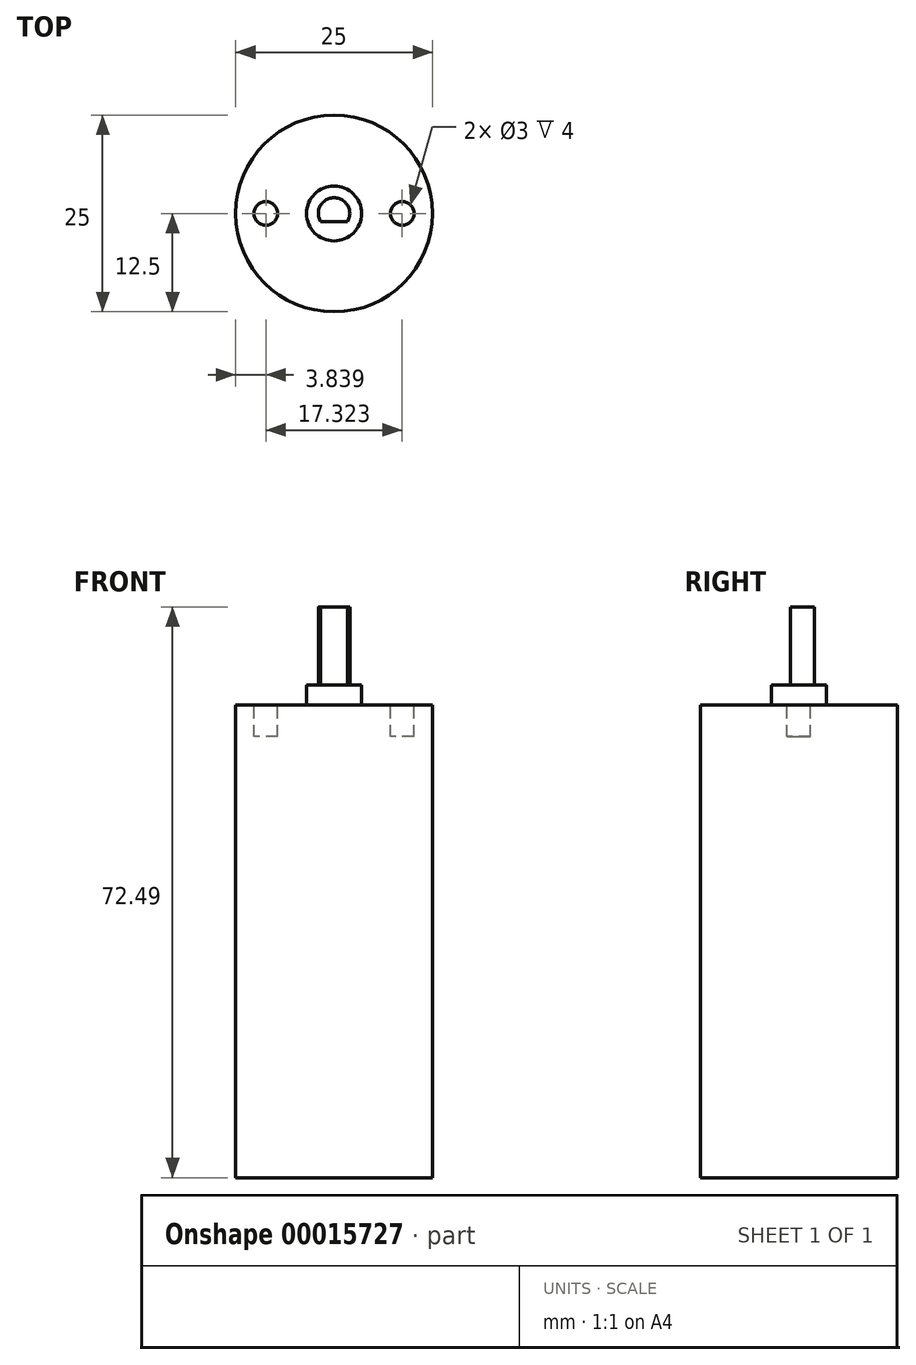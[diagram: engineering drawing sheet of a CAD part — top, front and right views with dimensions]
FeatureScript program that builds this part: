
annotation { "Feature Type Name" : "Feature", "Feature Type Description" : "" }
export const myFeature = defineFeature(function(context is Context, id is Id, definition is map)
    precondition{}
    {
        {
            var Q0;
            Q0=qCreatedBy(makeId("Top.planeOp"),FACE);
            var sketch = newSketch(context, id + "F0", { "sketchPlane" : qUnion([Q0])});
            skCircle(sketch, "E0", {"center": v(0, 0) * mm, "radius": 12.5 * mm});
            skSolve(sketch);
        }
        {
            var Q0;
            Q0=qSketchRegion(id+"F0",true);
            extrude(context, id + "F1", {"entities" : qUnion([Q0]), "depth" : 60.02 * mm});
        }
        {
            var Q0;
            Q0=makeQuery(id+"F1.opExtrude","CAP_FACE",FACE,{"disambiguationData":[OSD([sQuery(id+"F0.wireOp",EDGE,"E0")])],"isStart":false});
            var sketch = newSketch(context, id + "F2", { "sketchPlane" : qUnion([Q0])});
            skCircle(sketch, "E1", {"center": v(0, 0) * mm, "radius": 3.5 * mm});
            skSolve(sketch);
        }
        {
            var Q0;
            Q0=qSketchRegion(id+"F2",true);
            extrude(context, id + "F3", {"entities" : qUnion([Q0]), "operationType" : NewBodyOperationType.ADD, "depth" : 2.54 * mm});
        }
        {
            var Q0;
            Q0=makeQuery(id+"F1.opExtrude","CAP_FACE",FACE,{"disambiguationData":[OSD([sQuery(id+"F0.wireOp",EDGE,"E0")])],"isStart":false});
            var sketch = newSketch(context, id + "F4", { "sketchPlane" : qUnion([Q0])});
            skLineSegment(sketch, "E2", {"start": v(-8.66, 0) * mm, "end": v(8.66, 0) * mm, "construction": true});
            skPoint(sketch, "E3", {"position": v(0, 0) * mm});
            skCircle(sketch, "E4", {"center": v(-8.66, 0) * mm, "radius": 1.5 * mm});
            skCircle(sketch, "E5", {"center": v(8.66, 0) * mm, "radius": 1.5 * mm});
            skSolve(sketch);
        }
        {
            var Q0;
            Q0=qSketchRegion(id+"F4",true);
            extrude(context, id + "F5", {"entities" : qUnion([Q0]), "operationType" : NewBodyOperationType.REMOVE, "oppositeDirection" : true, "depth" : 4 * mm});
        }
        {
            var Q0;
            Q0=makeQuery(id+"F3.opExtrude","CAP_FACE",FACE,{"disambiguationData":[OSD([sQuery(id+"F2.wireOp",EDGE,"E1")])],"isStart":false});
            var sketch = newSketch(context, id + "F6", { "sketchPlane" : qUnion([Q0])});
            skCircle(sketch, "E6", {"center": v(0, 0) * mm, "radius": 2 * mm});
            skSolve(sketch);
        }
        {
            var Q0;
            Q0 = qSketchRegion(id + "F6", true);
            extrude(context, id + "F7", {"entities" : qUnion([Q0]), "operationType" : NewBodyOperationType.ADD, "depth" : 9.93 * mm});
        }
        {
            var Q0;
            Q0=makeQuery(id+"F7.opExtrude","CAP_FACE",FACE,{"disambiguationData":[OSD([sQuery(id+"F6.wireOp",EDGE,"E6")])],"isStart":false});
            var sketch = newSketch(context, id + "F8", { "sketchPlane" : qUnion([Q0])});
            skLineSegment(sketch, "E7.bottom", {"start": v(1.7, -1.05) * mm, "end": v(-1.7, -1.05) * mm});
            skLineSegment(sketch, "E7.top", {"start": v(1.7, -2) * mm, "end": v(-1.7, -2) * mm});
            skLineSegment(sketch, "E7.left", {"start": v(1.7, -1.05) * mm, "end": v(1.7, -2) * mm});
            skLineSegment(sketch, "E7.right", {"start": v(-1.7, -1.05) * mm, "end": v(-1.7, -2) * mm});
            skSolve(sketch);
        }
        {
            var Q0;
            Q0 = qSketchRegion(id + "F8", true);
            var Q1;
            Q1=makeQuery(id+"F3.opExtrude","CAP_FACE",FACE,{"disambiguationData":[OSD([sQuery(id+"F2.wireOp",EDGE,"E1")])],"isStart":false});
            extrude(context, id + "F9", {"entities" : qUnion([Q0]), "operationType" : NewBodyOperationType.REMOVE, "endBound" : BoundingType.UP_TO_SURFACE, "oppositeDirection" : true, "endBoundEntityFace" : qUnion([Q1]), "depth" : 25.4 * mm});
        }
    });
